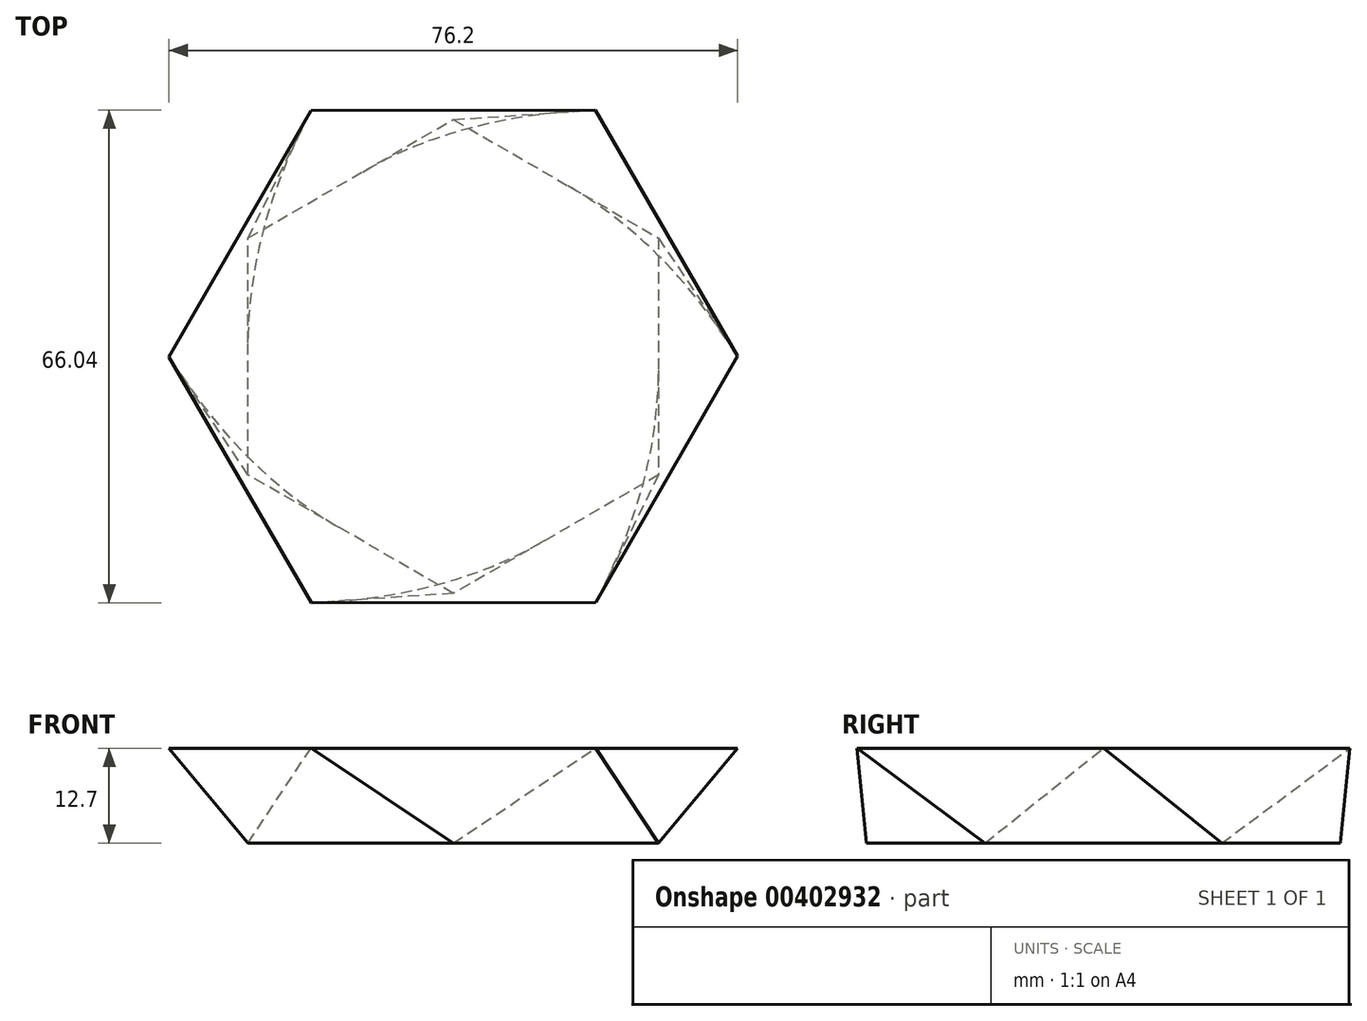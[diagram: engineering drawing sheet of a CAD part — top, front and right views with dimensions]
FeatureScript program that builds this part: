
annotation { "Feature Type Name" : "Feature", "Feature Type Description" : "" }
export const myFeature = defineFeature(function(context is Context, id is Id, definition is map)
    precondition{}
    {
        {
            var Q0;
            Q0=qCreatedBy(makeId("Top.planeOp"),FACE);
            var sketch = newSketch(context, id + "F0", { "sketchPlane" : qUnion([Q0])});
            skCircle(sketch, "E0.cCircle", {"center": v(0, 0) * mm, "radius": 27.5 * mm, "construction": true});
            skLineSegment(sketch, "E0.0", {"start": v(27.5, 15.87) * mm, "end": v(27.5, -15.87) * mm});
            skLineSegment(sketch, "E0.1", {"start": v(27.5, -15.87) * mm, "end": v(0, -31.75) * mm});
            skLineSegment(sketch, "E0.2", {"start": v(0, -31.75) * mm, "end": v(-27.5, -15.87) * mm});
            skLineSegment(sketch, "E0.3", {"start": v(-27.5, -15.87) * mm, "end": v(-27.5, 15.87) * mm});
            skLineSegment(sketch, "E0.4", {"start": v(-27.5, 15.87) * mm, "end": v(0, 31.75) * mm});
            skLineSegment(sketch, "E0.5", {"start": v(0, 31.75) * mm, "end": v(27.5, 15.87) * mm});
            skPoint(sketch, "E0.0.midPoint", {"position": v(27.5, 0) * mm});
            skSolve(sketch);
        }
        {
            var Q0;
            Q0=qCreatedBy(makeId("Top.planeOp"),FACE);
            cPlane(context, id + "F1", {"entities" : qUnion([Q0]), "cplaneType" : CPlaneType.OFFSET, "offset" : 12.7 * mm, "width" : 152.4 * mm, "height" : 152.4 * mm});
        }
        {
            var Q0;
            Q0=qCreatedBy(id+"F1.planeOp",FACE);
            var sketch = newSketch(context, id + "F2", { "sketchPlane" : qUnion([Q0])});
            skCircle(sketch, "E1.cCircle", {"center": v(0, 0) * mm, "radius": 33 * mm, "construction": true});
            skLineSegment(sketch, "E1.0", {"start": v(38.1, 0.05) * mm, "end": v(19.1, -32.97) * mm});
            skLineSegment(sketch, "E1.1", {"start": v(19.1, -32.97) * mm, "end": v(-19, -33.02) * mm});
            skLineSegment(sketch, "E1.2", {"start": v(-19, -33.02) * mm, "end": v(-38.1, -0.05) * mm});
            skLineSegment(sketch, "E1.3", {"start": v(-38.1, -0.05) * mm, "end": v(-19.1, 32.97) * mm});
            skLineSegment(sketch, "E1.4", {"start": v(-19.1, 32.97) * mm, "end": v(19, 33.02) * mm});
            skLineSegment(sketch, "E1.5", {"start": v(19, 33.02) * mm, "end": v(38.1, 0.05) * mm});
            skPoint(sketch, "E1.0.midPoint", {"position": v(28.6, -16.46) * mm});
            skSolve(sketch);
        }
        {
            var Q0;
            Q0=makeQuery(id+"F0.imprint","IMPRINT",FACE,{"disambiguationData":[TD([[makeQuery(id+"F0.imprint","IMPRINT",EDGE,{"derivedFrom":sQuery(id+"F0.wireOp",EDGE,"E0.0")}),-1.0]])]});
            var Q1;
            Q1=makeQuery(id+"F2.imprint","IMPRINT",FACE,{"disambiguationData":[TD([[makeQuery(id+"F2.imprint","IMPRINT",EDGE,{"derivedFrom":sQuery(id+"F2.wireOp",EDGE,"E1.0")}),-1.0]])]});
            loft(context, id + "F3", {"sheetProfilesArray" : [{ "sheetProfileEntities" : qUnion([Q0]) }, { "sheetProfileEntities" : qUnion([Q1]) }]});
        }
    });
